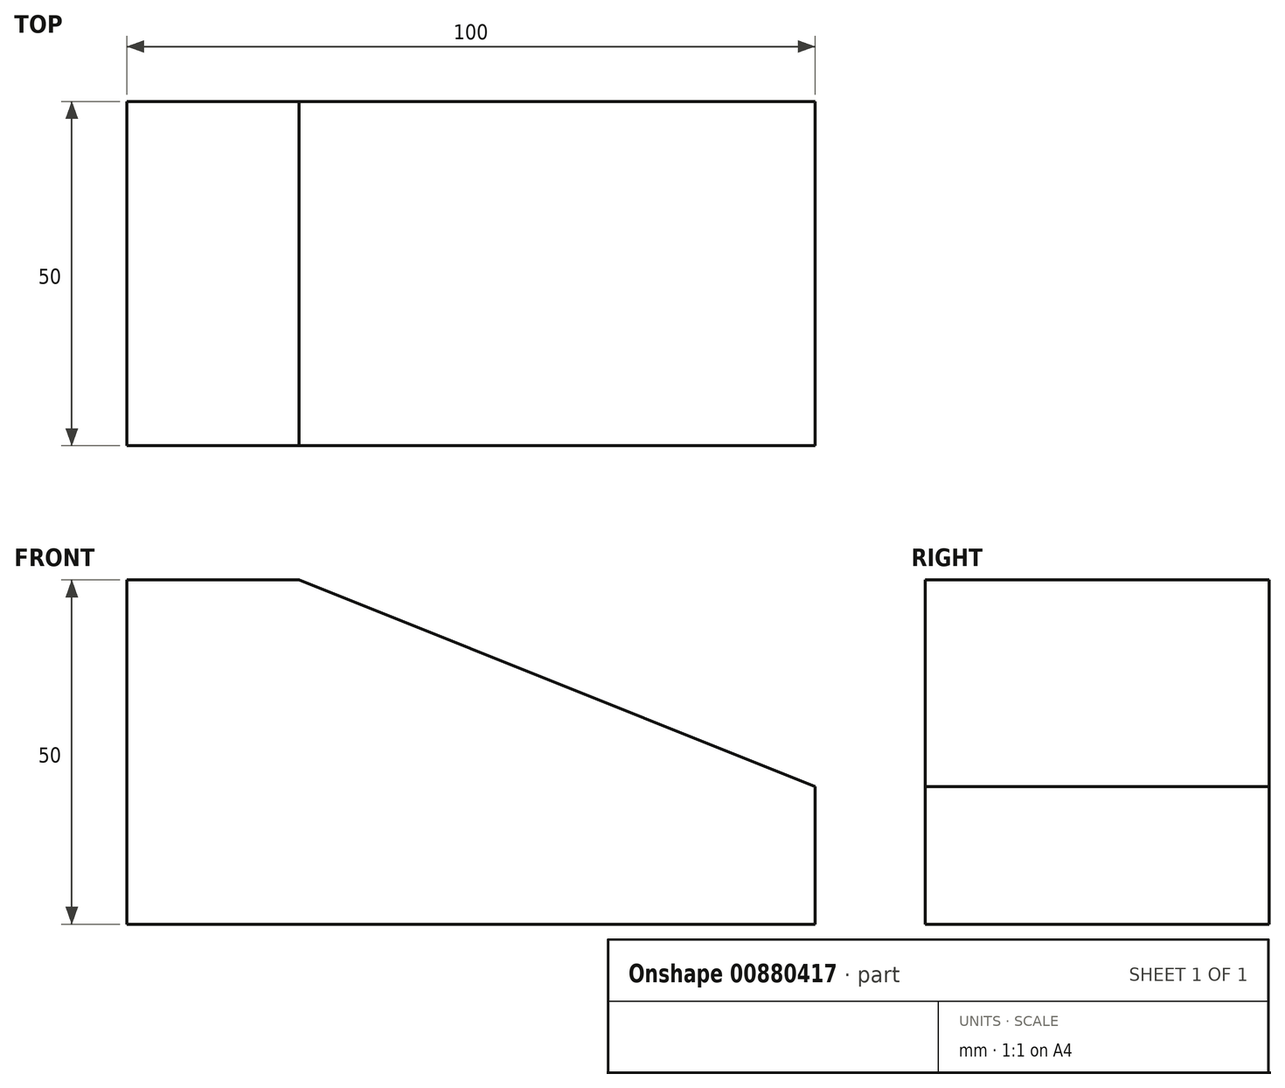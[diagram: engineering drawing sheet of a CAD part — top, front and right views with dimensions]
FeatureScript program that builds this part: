
annotation { "Feature Type Name" : "Feature", "Feature Type Description" : "" }
export const myFeature = defineFeature(function(context is Context, id is Id, definition is map)
    precondition{}
    {
        {
            var Q0;
            Q0=qCreatedBy(makeId("Front.planeOp"),FACE);
            var sketch = newSketch(context, id + "F0", { "sketchPlane" : qUnion([Q0])});
            skLineSegment(sketch, "E0", {"start": v(0, 0) * mm, "end": v(100, 0) * mm});
            skLineSegment(sketch, "E1", {"start": v(100, 0) * mm, "end": v(100, 20) * mm});
            skLineSegment(sketch, "E2", {"start": v(100, 20) * mm, "end": v(25, 50) * mm});
            skLineSegment(sketch, "E3", {"start": v(25, 50) * mm, "end": v(0, 50) * mm});
            skLineSegment(sketch, "E4", {"start": v(0, 50) * mm, "end": v(0, 0) * mm});
            skSolve(sketch);
        }
        {
            var Q0;
            Q0=makeQuery(id+"F0.imprint","IMPRINT",FACE,{"disambiguationData":[TD([[makeQuery(id+"F0.imprint","IMPRINT",EDGE,{"derivedFrom":sQuery(id+"F0.wireOp",EDGE,"E0")}),1.0]])]});
            extrude(context, id + "F1", {"entities" : qUnion([Q0]), "depth" : 50 * mm, "offsetDistance" : 25 * mm});
        }
    });
